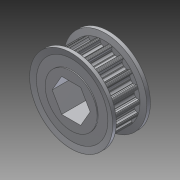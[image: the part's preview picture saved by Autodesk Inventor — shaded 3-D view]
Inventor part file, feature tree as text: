
AUTODESK INVENTOR PART (.ipt)
format: ipt  version: 2014 SP1 (Build 180222100, 222)  size: 689,664 bytes
history: native  units: in
note: dims shown in document units (in); Inventor stores cm internally (conversion verified against a paired STEP export)
features: mirror x1, other x1, imported_body x1
ambient origin geometry x8: Origin, YZ Plane, XZ Plane, XY Plane, X Axis, Y Axis, Z Axis, Center Point
bodies: Body1 (feature_tree)
feature tree (3):
  mirror  "Mirror1"
  other  "217-3225-STEP1"
  imported_body  "Base1"
